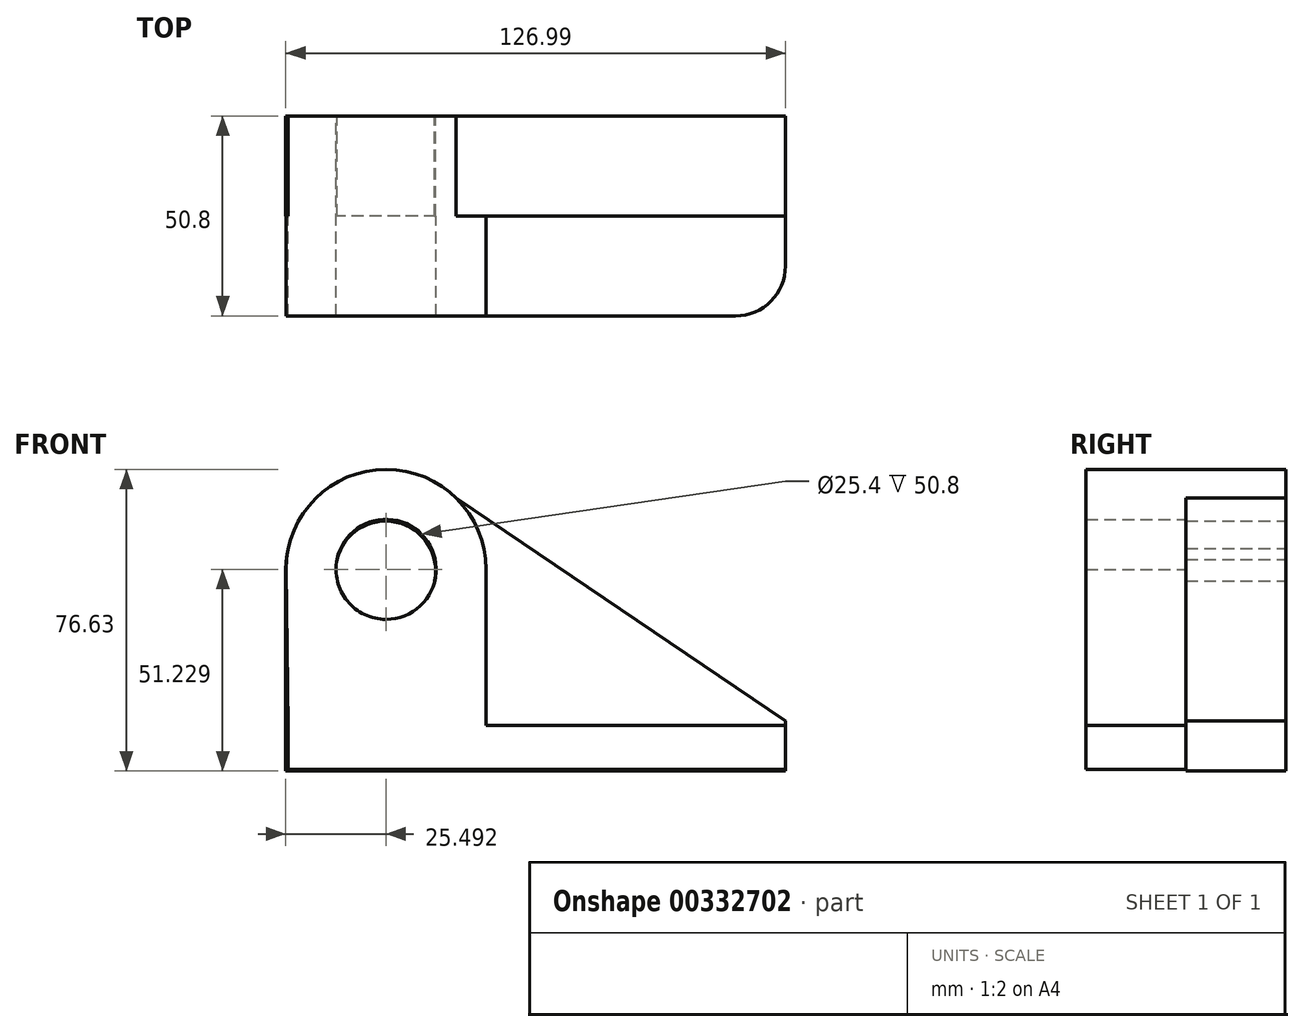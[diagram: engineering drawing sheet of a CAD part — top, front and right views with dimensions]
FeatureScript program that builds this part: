
annotation { "Feature Type Name" : "Feature", "Feature Type Description" : "" }
export const myFeature = defineFeature(function(context is Context, id is Id, definition is map)
    precondition{}
    {
        {
            var Q0;
            Q0=qCreatedBy(makeId("Front.planeOp"),FACE);
            var sketch = newSketch(context, id + "F0", { "sketchPlane" : qUnion([Q0])});
            skCircle(sketch, "E0", {"center": v(-37.37, 27.84) * mm, "radius": 12.7 * mm});
            skArc(sketch, "E1", {"start": v(-23.13, 48.87) * mm, "mid": v(-49.28, 50.27) * mm, "end": v(-62.77, 27.84) * mm});
            skLineSegment(sketch, "E2", {"start": v(-62.77, 27.84) * mm, "end": v(-62.77, -22.96) * mm});
            skLineSegment(sketch, "E3", {"start": v(-62.77, -22.96) * mm, "end": v(64.23, -22.96) * mm});
            skLineSegment(sketch, "E4", {"start": v(64.22, -22.96) * mm, "end": v(64.22, -10.26) * mm});
            skLineSegment(sketch, "E5", {"start": v(64.22, -10.26) * mm, "end": v(-23.13, 48.87) * mm});
            skSolve(sketch);
        }
        {
            var Q0;
            Q0=makeQuery(id+"F0.imprint","IMPRINT",FACE,{"disambiguationData":[TD([[makeQuery(id+"F0.imprint","IMPRINT",EDGE,{"derivedFrom":sQuery(id+"F0.wireOp",EDGE,"E0")}),-1.0]])]});
            extrude(context, id + "F1", {"entities" : qUnion([Q0]), "depth" : 25.4 * mm});
        }
        {
            var Q0;
            Q0=qCreatedBy(makeId("Front.planeOp"),FACE);
            var sketch = newSketch(context, id + "F2", { "sketchPlane" : qUnion([Q0])});
            skCircle(sketch, "E6", {"center": v(-37.28, 28.27) * mm, "radius": 12.7 * mm});
            skArc(sketch, "E7", {"start": v(-11.88, 28.27) * mm, "mid": v(-37.28, 53.67) * mm, "end": v(-62.68, 28.27) * mm});
            skLineSegment(sketch, "E8.bottom", {"start": v(64.2, -11.43) * mm, "end": v(-11.88, -11.43) * mm});
            skLineSegment(sketch, "E8.top", {"start": v(64.2, -22.53) * mm, "end": v(-62.18, -22.53) * mm});
            skLineSegment(sketch, "E8.left", {"start": v(64.2, -11.43) * mm, "end": v(64.2, -22.53) * mm});
            skLineSegment(sketch, "E8.right", {"start": v(-62.18, -11.43) * mm, "end": v(-62.18, -22.53) * mm});
            skLineSegment(sketch, "E9", {"start": v(-11.88, 28.27) * mm, "end": v(-11.88, -11.43) * mm});
            skLineSegment(sketch, "E10", {"start": v(-62.68, 28.27) * mm, "end": v(-62.18, -11.43) * mm});
            skSolve(sketch);
        }
        {
            var Q0;
            Q0=makeQuery(id+"F2.imprint","IMPRINT",FACE,{"disambiguationData":[TD([[makeQuery(id+"F2.imprint","IMPRINT",EDGE,{"derivedFrom":sQuery(id+"F2.wireOp",EDGE,"E6")}),-1.0]])]});
            extrude(context, id + "F3", {"entities" : qUnion([Q0]), "operationType" : NewBodyOperationType.ADD, "depth" : 50.8 * mm});
        }
        {
            var Q0;
            Q0=makeQuery(id+"F3.opExtrude","CAP_EDGE",EDGE,{"disambiguationData":[OSD([sQuery(id+"F2.wireOp",EDGE,"E8.left")])],"isStart":false});
            fillet(context, id + "F4", {"entities" : qUnion([Q0]), "radius" : 12.7 * mm, "tangentPropagation" : true, "allowEdgeOverflow" : false});
        }
    });
